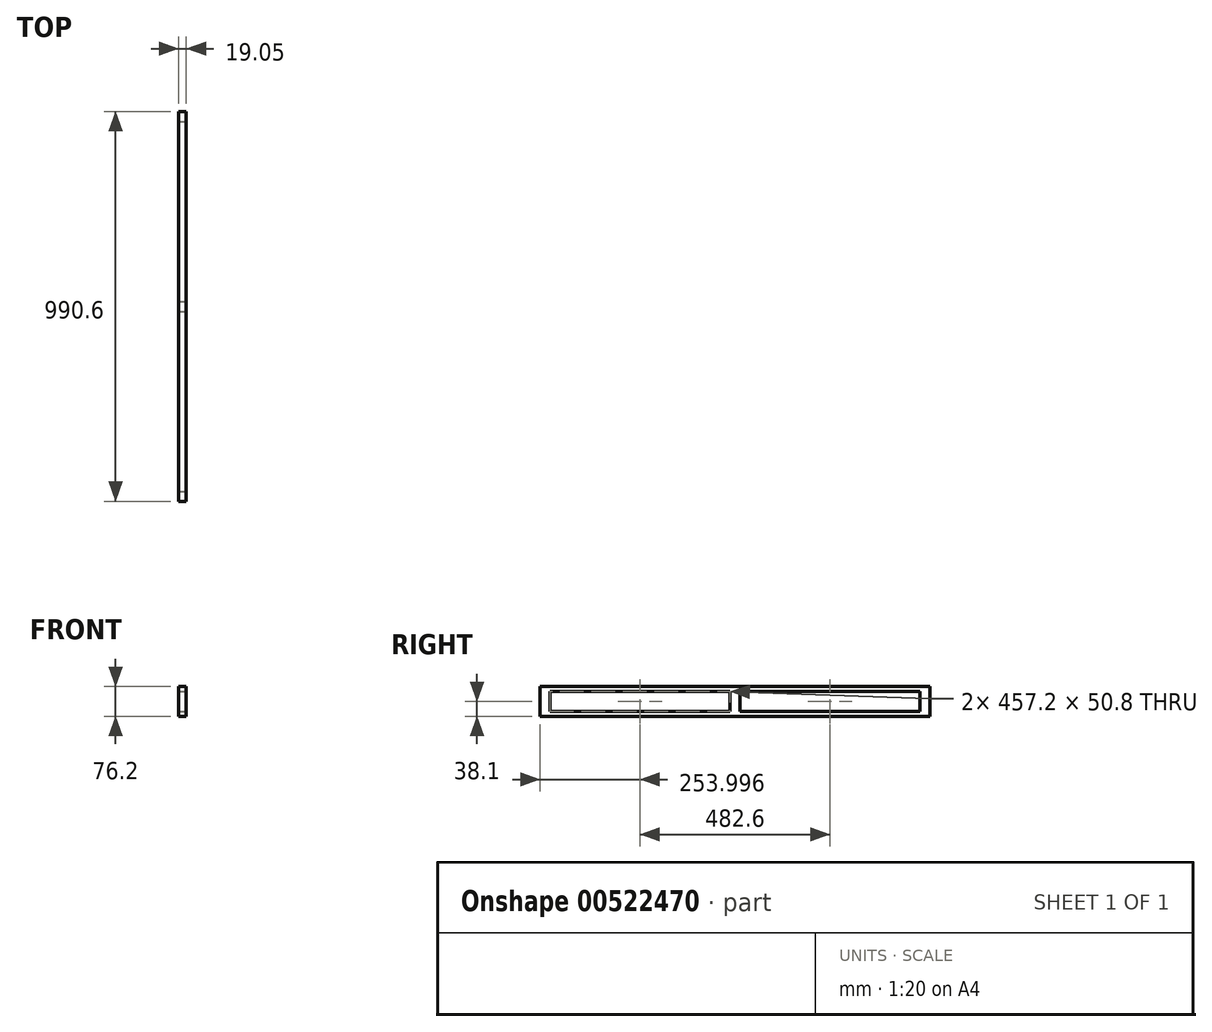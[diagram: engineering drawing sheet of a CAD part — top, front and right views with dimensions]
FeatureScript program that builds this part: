
annotation { "Feature Type Name" : "Feature", "Feature Type Description" : "" }
export const myFeature = defineFeature(function(context is Context, id is Id, definition is map)
    precondition{}
    {
        {
            var Q0;
            Q0=qCreatedBy(makeId("Top.planeOp"),FACE);
            var sketch = newSketch(context, id + "F0", { "sketchPlane" : qUnion([Q0])});
            skLineSegment(sketch, "E0.bottom", {"start": v(0, 587.79) * mm, "end": v(19.05, 587.79) * mm});
            skLineSegment(sketch, "E0.top", {"start": v(0, -402.81) * mm, "end": v(19.05, -402.81) * mm});
            skLineSegment(sketch, "E0.left", {"start": v(0, 587.79) * mm, "end": v(0, -402.81) * mm});
            skLineSegment(sketch, "E0.right", {"start": v(19.05, 587.79) * mm, "end": v(19.05, -402.81) * mm});
            skSolve(sketch);
        }
        {
            var Q0;
            Q0=makeQuery(id+"F0.imprint","IMPRINT",FACE,{"disambiguationData":[TD([[makeQuery(id+"F0.imprint","IMPRINT",EDGE,{"derivedFrom":sQuery(id+"F0.wireOp",EDGE,"E0.bottom")}),-1.0]])]});
            extrude(context, id + "F1", {"entities" : qUnion([Q0]), "depth" : 76.2 * mm, "offsetDistance" : 25.4 * mm});
        }
        {
            var Q0;
            Q0=makeQuery(id+"F1.opExtrude","SWEPT_FACE",FACE,{"disambiguationData":[OSD([sQuery(id+"F0.wireOp",EDGE,"E0.right")])]});
            var sketch = newSketch(context, id + "F2", { "sketchPlane" : qUnion([Q0])});
            skLineSegment(sketch, "E1.bottom", {"start": v(-377.41, 63.5) * mm, "end": v(79.79, 63.5) * mm});
            skLineSegment(sketch, "E1.top", {"start": v(-377.41, 12.7) * mm, "end": v(79.79, 12.7) * mm});
            skLineSegment(sketch, "E1.left", {"start": v(-377.41, 63.5) * mm, "end": v(-377.41, 12.7) * mm});
            skLineSegment(sketch, "E1.right", {"start": v(79.79, 63.5) * mm, "end": v(79.79, 12.7) * mm});
            skLineSegment(sketch, "E2.bottom", {"start": v(562.39, 63.5) * mm, "end": v(105.19, 63.5) * mm});
            skLineSegment(sketch, "E2.top", {"start": v(562.39, 12.7) * mm, "end": v(105.19, 12.7) * mm});
            skLineSegment(sketch, "E2.left", {"start": v(562.39, 63.5) * mm, "end": v(562.39, 12.7) * mm});
            skLineSegment(sketch, "E2.right", {"start": v(105.19, 63.5) * mm, "end": v(105.19, 12.7) * mm});
            skSolve(sketch);
        }
        {
            var Q0;
            Q0=qSketchRegion(id+"F2",true);
            extrude(context, id + "F3", {"entities" : qUnion([Q0]), "operationType" : NewBodyOperationType.REMOVE, "oppositeDirection" : true, "depth" : 25.4 * mm, "offsetDistance" : 25.4 * mm});
        }
    });
